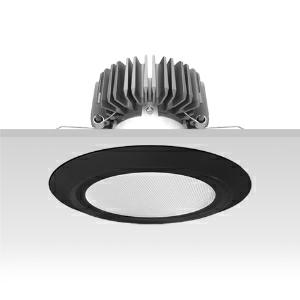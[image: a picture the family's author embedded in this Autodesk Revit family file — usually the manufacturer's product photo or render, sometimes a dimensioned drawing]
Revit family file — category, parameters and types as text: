
# Revit family: 3f_filippi_-_3f_reno_bianco_ampio_3f_filippi_-_30637_a01049_-_3f_reno_200_wh_4000-840_wide___smp_bk_9820
name_source: partatom
category: Lighting Fixtures
units: mm (PartAtom-declared; Revit-internal decimal feet)

## family parameters
Cut with Voids When Loaded = No
Host = Face
Light Source = No
Part Type = Normal
Room Calculation Point = No
Round Connector Dimension = Use Diameter
Shared = No

## types (1)
- 3F Filippi - 3F Reno Bianco Ampio (1 x LED, 3089 lm, 36 W, 4000 K)
    Apparent Load = 36 VA
    Approval mark = CE
    CIE Flux Codes = 74 92 98 100 100
    Color Rendering = 80
    Color Temperature = 4000 K
    Control Gear = Electronic ballast
    Default Elevation = 1800 mm
    Description = ILLUMINOTECHNICAL
Luminous efficiency 100% (DLOR 100%, ULOR 0%).
Initial luminous flux of the luminaire 3089 lm.
Direct symmetric wide distribution.
Installation Interdistance Transv.D = 1.06 x hu - Long.D = 1.04 x hu.
Tabular UGR (CIE 117 - 4H-8H; S=0.25H; 70/50/20): RUG 23.5 - 23.3.
Beam angle: 70° - 69°.
Luminous efficacy 86 lm/W.
Lifetime (L90/B10): 30000 h. (tq+25°C)
Lifetime (L85/B10): 50000 h. (tq+25°C)
Lifetime (L70/B10): 80000 h. (tq+25°C)
Sudden decreased luminous flux after 50000 hours: 0% (C0).
Photobiological safety in compliance with IEC/TR 62778: RG1 low risk, (IEC 62471).
In compliance with IEC/EN 62722-2-1 - IEC/EN 62717 standards.

SOURCE
Compact LED module 4000/840.
Energy efficiency class (UE 2019/2020 - UE 2019/2015): E.
CIE 13.3 Colour rendering index: CRI >80 (R9 <50%).
IES TM-30 Fidelity Index: Rf = 84 Rg = 95.
CCT nominal colour temperature 4000 K.
Colour initial tolerance (MacAdam): SDCM 3.
Zhaga Book 3 compliant.

MECHANICAL
Passive heat dissipator in die-casting aluminium, oversized, for optimum thermal management of the LED module.
Parabolic element with graduated/concentric rings in white polycarbonate.
Transparent external lens with glossy and satin differentiated surfaces, with a cooling and anti-insect system in methacrylate (PMMA).
Fastening spring clips in stainless steel.
Dimensions: diameter 226 mm, height 146 mm. Weight 1.655 kg.
IP44 protection degree for exposed part, IP20 for recessed part.
Mechanical strength to impacts IK05 (0.7 joule).
Glow-wire test resistance 650°C.

ELECTRICAL
Wiring on a separate unit.
Halogen Free electronic wiring 230V-50/60Hz, power factor 0.95, THD <25%, constant output current, SELV, class II, 1 driver.
Power of the luminaire 36 W.
ENEC - CE.
SAFE FLICKER: PstLM=<1 and SVM=<0.4 (IEC TR 61547-1 and IEC TR 63158), to ensure a more comfortable and safe light.
Luminaire compliant with EN 60598-2-22 for power supply from a centralised emergency system CPSS (Central Power Supply System), not incorporated in the luminaire - high risk areas excluded. The default power and flux are 100% in AC and 100% in DC.
Ambient temperature from 0°C to +25°C.
Temperature class T6 max 85°C.
Relative humidity UR: <85%.

INSTALLATION
Pull-up recessed fitting.
False ceiling carving: 200 mm.
All accessories dedicated to this product are available on the Catalog and on our website www.3F-Filippi.com.

ACCESSORIES
A01049 - Anti-glare microprismatic SMP diffuser in methacrylate (PMMA), locked and in line with the trim, in black polycarbonate.

APPLICATIONS
Suitable product for food production plants (HACCP), IFS (Food Version 6), BRC (GSFS Food Version 7).
Environments: architectural, commercial, exhibition areas, transit areas, corridors, shops, display windows, service areas.
In false ceilings with narrow voids.

WARNING
Luminaire designed for disposal/recycling at end-of-life.
Replaceable (LED only) light source by a professional. Replaceable control gear by a professional.
    Height = 0 mm  [stored 0 ft]
    Lamp = 1 x LED
    Lamp Light Flux = 3089 lm
    Lamp Power = 36 W
    Lamp count = 1
    Length = 226 mm
    Lifetime = 50000 h
    Luminous efficacy = 86 lm/W
    Manufacturer = 3F Filippi
    ModVariant = No
    Model = 3F Filippi - 30637+A01049 - 3F Reno 200 WH 4000-840 WIDE + SMP BK
    Mounting Place = Ceiling
    Mounting Type = Recessed
    Number of Poles = 1
    OnlyDefault = Yes
    Power Factor = 1
    Product Name = 3F Filippi - 3F Reno Bianco Ampio
    Product group = recessed luminaire
    ProductGroupID = 4
    Protection Class = Protection class II
    Protection Degree = IP 20
    RLX_Detail_Level = 1
    RLX_Emergency_Light_Flux = 0 lm
    RLX_Emergency_Type = 0
    RLX_Emergency_Type_DB = No
    RlxData = <blob elided: 97809 chars, md5=343bc3fa>
    Socket = socket
    Standby Power = 0 W
    System Light Flux = 3089 lm
    System Power = 36 W
    Type Comments = Product without accessories
    Type Image = 3ffilippi_3f_reno_200_bk_vs_smp.jpg
    URL = http://relux.com
    VarID = ---
    Voltage = 0 V
    Weight = 0.00 kg
    Width = 0 mm  [stored 0 ft]

note: [stored X ft] marks values corroborated as IEEE doubles in the binary element streams (Revit-internal decimal feet)

## geometry (parser evidence)
native form markers: Blend x4, Sweep x11
no freeform markers — native parametric forms only
